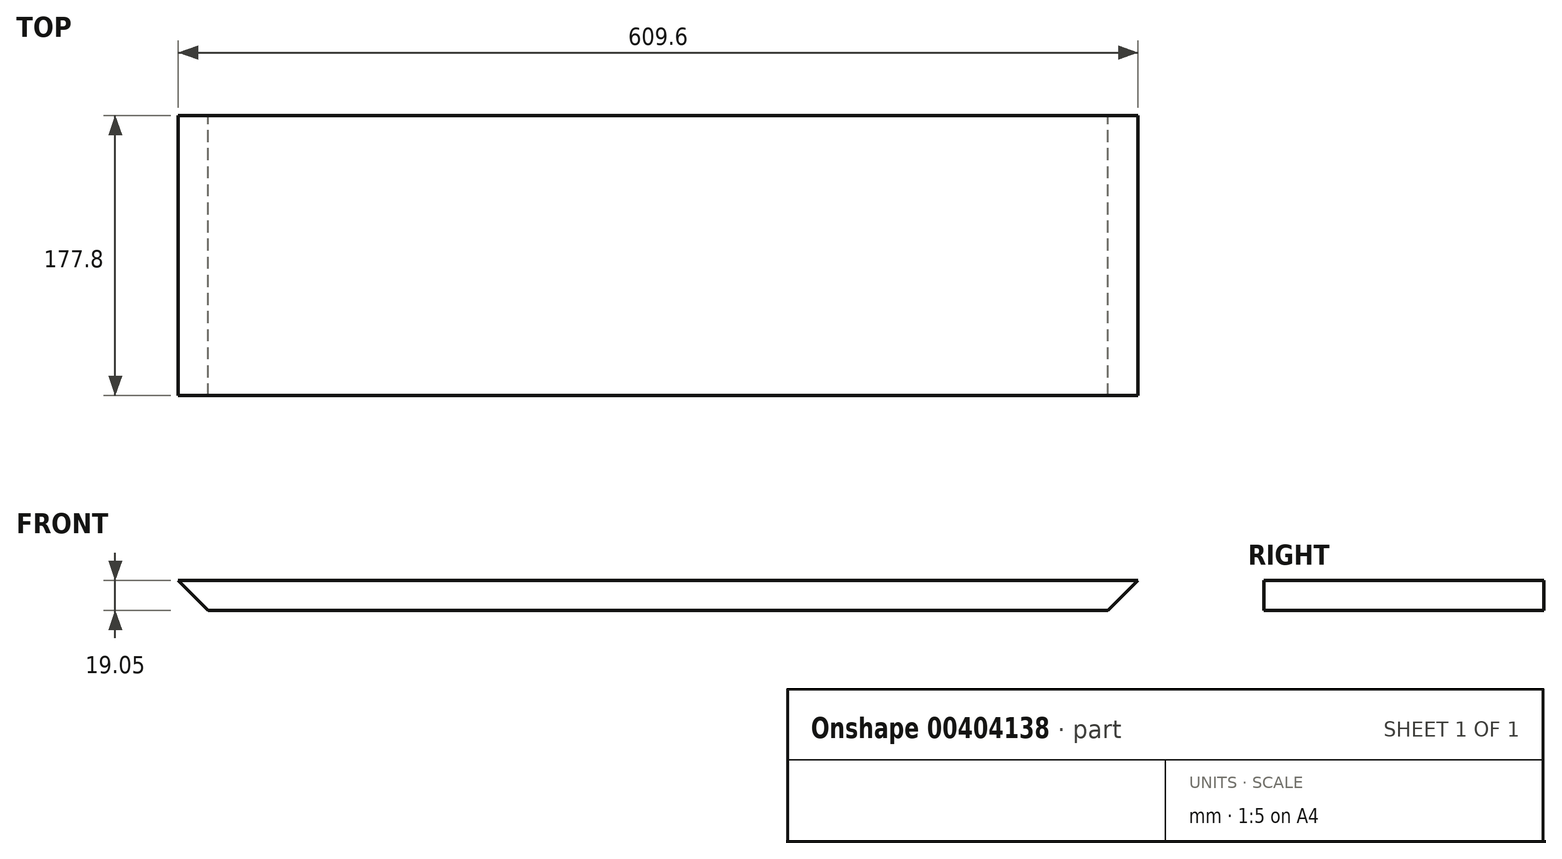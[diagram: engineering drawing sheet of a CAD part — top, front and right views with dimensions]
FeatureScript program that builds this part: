
annotation { "Feature Type Name" : "Feature", "Feature Type Description" : "" }
export const myFeature = defineFeature(function(context is Context, id is Id, definition is map)
    precondition{}
    {
        {
            var Q0;
            Q0=qCreatedBy(makeId("Front.planeOp"),FACE);
            var sketch = newSketch(context, id + "F0", { "sketchPlane" : qUnion([Q0])});
            skLineSegment(sketch, "E0", {"start": v(19.05, -19.81) * mm, "end": v(590.55, -19.81) * mm});
            skLineSegment(sketch, "E1.MirrorCS", {"start": v(0, -0.76) * mm, "end": v(19.05, -19.81) * mm});
            skLineSegment(sketch, "E2.MirrorCS", {"start": v(0, -0.76) * mm, "end": v(609.6, -0.76) * mm});
            skLineSegment(sketch, "E3.MirrorCS", {"start": v(609.6, -0.76) * mm, "end": v(590.55, -19.81) * mm});
            skSolve(sketch);
        }
        {
            var Q0;
            Q0 = qSketchRegion(id + "F0", true);
            extrude(context, id + "F1", {"entities" : qUnion([Q0]), "endBound" : BoundingType.SYMMETRIC, "depth" : 177.8 * mm});
        }
    });
